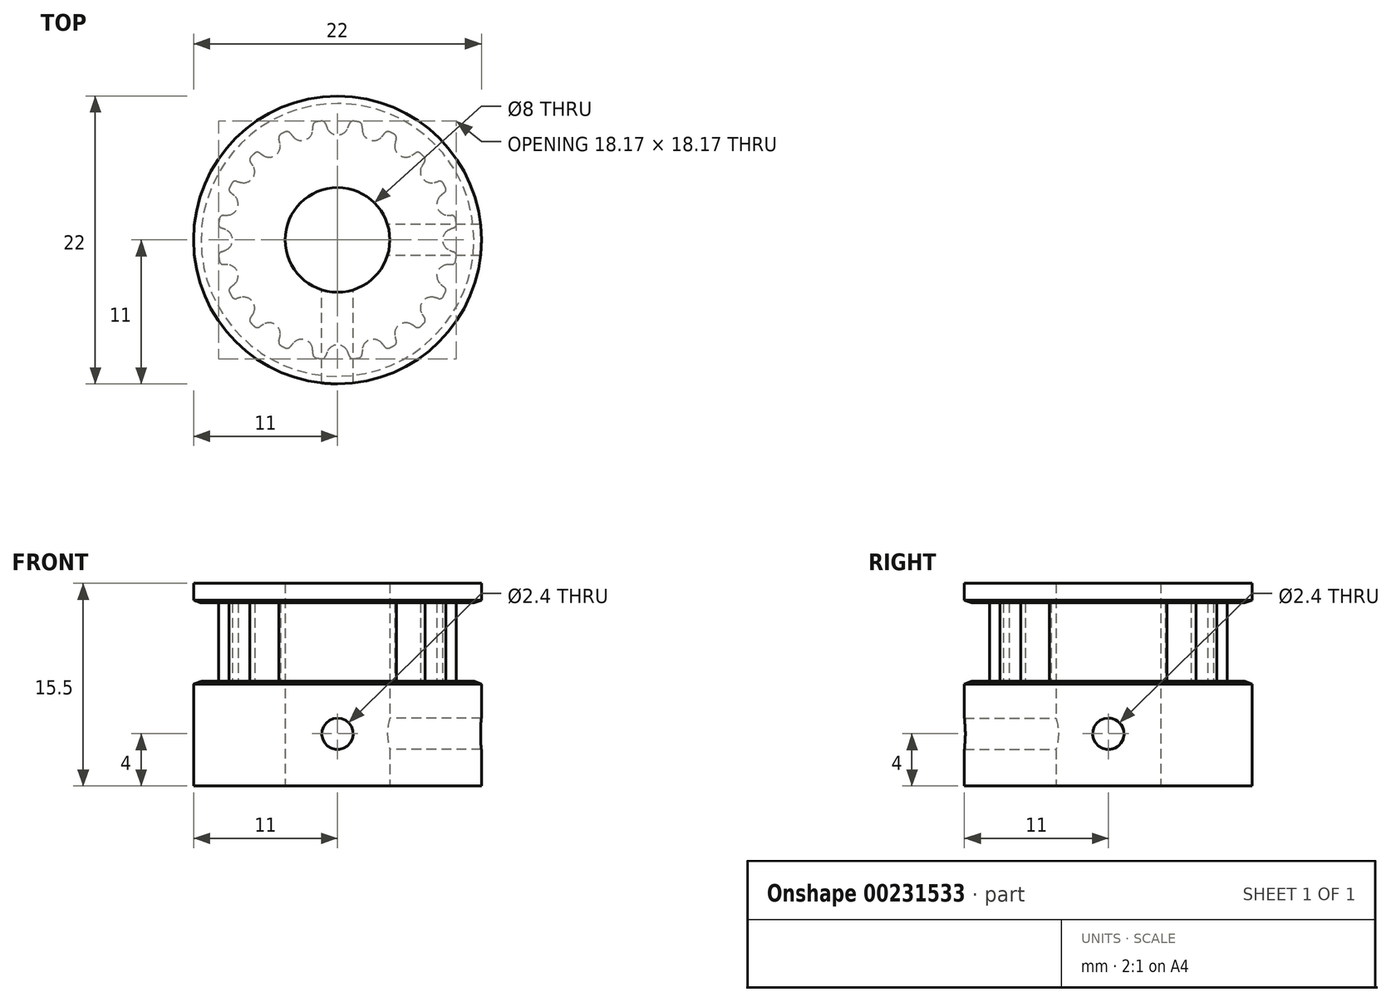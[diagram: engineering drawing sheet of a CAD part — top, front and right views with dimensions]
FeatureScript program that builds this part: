
annotation { "Feature Type Name" : "Feature", "Feature Type Description" : "" }
export const myFeature = defineFeature(function(context is Context, id is Id, definition is map)
    precondition{}
    {
        {
            assignVariable(context, id + "F0", {"name" : "teeth", "anyValue" : 20});
        }
        {
            assignVariable(context, id + "F1", {"name" : "belt_width", "anyValue" : 6 * mm});
        }
        {
            assignVariable(context, id + "F2", {"name" : "bore_diameter", "anyValue" : 8 * mm});
        }
        {
            var Q0;
            Q0=qCreatedBy(makeId("Top.planeOp"),FACE);
            var sketch = newSketch(context, id + "F3", { "sketchPlane" : qUnion([Q0])});
            skLineSegment(sketch, "E0", {"start": v(0, 0) * mm, "end": v(0, 8.03) * mm, "construction": true});
            skCircle(sketch, "E1", {"center": v(0, 0) * mm, "radius": 9.17 * mm});
            skPoint(sketch, "E2.MirrorCS.end.orphan", {"position": v(1.43, 9.06) * mm});
            skLineSegment(sketch, "E3", {"start": v(1.43, 9.06) * mm, "end": v(1.5, 9.43) * mm, "construction": true});
            skLineSegment(sketch, "E4", {"start": v(-1.43, 9.06) * mm, "end": v(-1.5, 9.43) * mm, "construction": true});
            skArc(sketch, "E5", {"start": v(0, 8.03) * mm, "mid": v(0.47, 8.17) * mm, "end": v(0.79, 8.55) * mm});
            skArc(sketch, "E6", {"start": v(0.79, 8.55) * mm, "mid": v(0.84, 8.72) * mm, "end": v(0.88, 8.89) * mm, "construction": true});
            skLineSegment(sketch, "E7", {"start": v(0, 8.03) * mm, "end": v(0, 9.17) * mm, "construction": true});
            skLineSegment(sketch, "E8", {"start": v(0, 9.17) * mm, "end": v(0, 9.55) * mm, "construction": true});
            skArc(sketch, "E9", {"start": v(0.88, 8.89) * mm, "mid": v(0.98, 9.05) * mm, "end": v(1.16, 9.1) * mm, "construction": true});
            skArc(sketch, "E10", {"start": v(1.5, 9.43) * mm, "mid": v(0, 9.55) * mm, "end": v(-1.5, 9.43) * mm, "construction": true});
            skLineSegment(sketch, "E11", {"start": v(1.43, 9.06) * mm, "end": v(1.26, 7.93) * mm});
            skLineSegment(sketch, "E12", {"start": v(1.26, 7.93) * mm, "end": v(0, 0) * mm});
            skLineSegment(sketch, "E13", {"start": v(0, 0) * mm, "end": v(-1.26, 7.93) * mm});
            skLineSegment(sketch, "E14", {"start": v(-1.26, 7.93) * mm, "end": v(-1.43, 9.06) * mm});
            skArc(sketch, "E15", {"start": v(1.25, 9.08) * mm, "mid": v(1.04, 9.04) * mm, "end": v(0.91, 8.88) * mm});
            skArc(sketch, "E16", {"start": v(0.79, 8.55) * mm, "mid": v(0.85, 8.72) * mm, "end": v(0.91, 8.88) * mm});
            skArc(sketch, "E17.MirrorCS", {"start": v(0, 8.03) * mm, "mid": v(-0.47, 8.17) * mm, "end": v(-0.79, 8.55) * mm});
            skArc(sketch, "E18.MirrorCS", {"start": v(-0.79, 8.55) * mm, "mid": v(-0.85, 8.72) * mm, "end": v(-0.91, 8.88) * mm});
            skArc(sketch, "E19.MirrorCS", {"start": v(-1.25, 9.08) * mm, "mid": v(-1.04, 9.04) * mm, "end": v(-0.91, 8.88) * mm});
            skArc(sketch, "E20", {"start": v(0, 9.17) * mm, "mid": v(-0.3, 9.16) * mm, "end": v(-0.61, 9.15) * mm});
            skArc(sketch, "E21", {"start": v(1.26, 7.93) * mm, "mid": v(0, 8.03) * mm, "end": v(-1.26, 7.93) * mm, "construction": true});
            skLineSegment(sketch, "E22", {"start": v(1.5, 9.43) * mm, "end": v(1.63, 10.3) * mm, "construction": true});
            skLineSegment(sketch, "E23", {"start": v(-1.5, 9.43) * mm, "end": v(-1.63, 10.3) * mm, "construction": true});
            skArc(sketch, "E24", {"start": v(1.63, 10.3) * mm, "mid": v(0, 10.43) * mm, "end": v(-1.63, 10.3) * mm, "construction": true});
            skSolve(sketch);
        }
        {
            var Q0;
            Q0=makeQuery(id+"F3.imprint","IMPRINT",FACE,{"disambiguationData":[TD([[makeQuery(id+"F3.imprint","IMPRINT",EDGE,{"derivedFrom":sQuery(id+"F3.wireOp",EDGE,"E5")}),-1.0]])]});
            var Q1;
            {var subQ1=sQuery(id+"F3.wireOp",EDGE,"E14");Q1=makeQuery(id+"F3.imprint","IMPRINT",FACE,{"disambiguationData":[TD([[makeQuery(id+"F3.imprint","IMPRINT",EDGE,{"derivedFrom":subQ1}),-1.0]])]});}
            var Q2;
            {var subQ0=sQuery(id+"F3.wireOp",EDGE,"E12");Q2=makeQuery(id+"F3.imprint","IMPRINT",FACE,{"disambiguationData":[TD([[makeQuery(id+"F3.imprint","IMPRINT",EDGE,{"derivedFrom":subQ0}),-1.0]])]});}
            extrude(context, id + "F4", {"entities" : qUnion([Q0, Q1, Q2]), "endBound" : BoundingType.SYMMETRIC, "depth" : getVariable(context, 'belt_width')});
        }
        {
            var Q0;
            Q0=makeQuery(id+"F4.opExtrude","SWEPT_BODY",BODY,{"disambiguationData":[OSD([sQuery(id+"F3.wireOp",EDGE,"E1"),sQuery(id+"F3.wireOp",EDGE,"E5"),sQuery(id+"F3.wireOp",EDGE,"E11"),sQuery(id+"F3.wireOp",EDGE,"E12"),sQuery(id+"F3.wireOp",EDGE,"E13"),sQuery(id+"F3.wireOp",EDGE,"E14"),sQuery(id+"F3.wireOp",EDGE,"E15"),sQuery(id+"F3.wireOp",EDGE,"E16"),sQuery(id+"F3.wireOp",EDGE,"E17.MirrorCS"),sQuery(id+"F3.wireOp",EDGE,"E18.MirrorCS"),sQuery(id+"F3.wireOp",EDGE,"E19.MirrorCS")])]});
            var Q1;
            Q1=makeQuery(id+"F4.opExtrude","SWEPT_EDGE",EDGE,{"disambiguationData":[OSD([sQuery(id+"F3.wireOp",EDGE,"E12"),sQuery(id+"F3.wireOp",EDGE,"E13")])]});
            circularPattern(context, id + "F5", {"operationType" : NewBodyOperationType.ADD, "entities" : qUnion([Q0]), "axis" : qUnion([Q1]), "angle" : 360 * degree, "instanceCount" : getVariable(context, 'teeth'), "equalSpace" : true});
        }
        {
            var Q0;
            Q0=qCreatedBy(makeId("Front.planeOp"),FACE);
            var sketch = newSketch(context, id + "F6", { "sketchPlane" : qUnion([Q0])});
            skLineSegment(sketch, "E25", {"start": v(0, -3) * mm, "end": v(10.43, -3) * mm});
            skLineSegment(sketch, "E26", {"start": v(10.43, -3) * mm, "end": v(11, -3.2) * mm});
            skLineSegment(sketch, "E27", {"start": v(11, -3.2) * mm, "end": v(11, -11) * mm});
            skLineSegment(sketch, "E28", {"start": v(11, -11) * mm, "end": v(0, -11) * mm});
            skLineSegment(sketch, "E29", {"start": v(0, -11) * mm, "end": v(0, -3) * mm});
            skLineSegment(sketch, "E30", {"start": v(0, 3) * mm, "end": v(10.43, 3) * mm});
            skLineSegment(sketch, "E31", {"start": v(11, 3.2) * mm, "end": v(10.43, 3) * mm});
            skLineSegment(sketch, "E32", {"start": v(11, 3.2) * mm, "end": v(11, 4.5) * mm});
            skLineSegment(sketch, "E33", {"start": v(11, 4.5) * mm, "end": v(0, 4.5) * mm});
            skLineSegment(sketch, "E34", {"start": v(0, 4.5) * mm, "end": v(0, 3) * mm});
            skLineSegment(sketch, "E35", {"start": v(10.43, -3) * mm, "end": v(11, -3) * mm, "construction": true});
            skLineSegment(sketch, "E36", {"start": v(11, -3) * mm, "end": v(11, -3.2) * mm, "construction": true});
            skLineSegment(sketch, "E37", {"start": v(10.43, 3) * mm, "end": v(11, 3) * mm, "construction": true});
            skLineSegment(sketch, "E38", {"start": v(11, 3) * mm, "end": v(11, 3.2) * mm, "construction": true});
            skLineSegment(sketch, "E39", {"start": v(9.17, -3) * mm, "end": v(9.17, 0) * mm, "construction": true});
            skSolve(sketch);
        }
        {
            var Q0;
            Q0=qSketchRegion(id+"F6",true);
            var Q1;
            Q1=qConstructionFilter(qBodyType(qCreatedBy(id+"F6",EDGE),BodyType.WIRE),ConstructionObject.NO);
            var Q2;
            Q2=sQuery(id+"F6.wireOp",EDGE,"E29");
            revolve(context, id + "F7", {"operationType" : NewBodyOperationType.ADD, "entities" : qUnion([Q0]), "surfaceEntities" : qUnion([Q1]), "axis" : qUnion([Q2]), "revolveType" : RevolveType.FULL});
        }
        {
            var Q0;
            Q0=makeQuery(id+"F7.opRevolve","SWEPT_FACE",FACE,{"disambiguationData":[OSD([sQuery(id+"F6.wireOp",EDGE,"E28")])]});
            var sketch = newSketch(context, id + "F8", { "sketchPlane" : qUnion([Q0])});
            skPoint(sketch, "E40", {"position": v(0, 0) * mm});
            skSolve(sketch);
        }
        {
            var Q0;
            Q0=sQuery(id+"F8.wireOp",VERTEX,"E40");
            var Q1;
            Q1=makeQuery(id+"F4.opExtrude","SWEPT_BODY",BODY,{"disambiguationData":[OSD([sQuery(id+"F3.wireOp",EDGE,"E1"),sQuery(id+"F3.wireOp",EDGE,"E5"),sQuery(id+"F3.wireOp",EDGE,"E11"),sQuery(id+"F3.wireOp",EDGE,"E12"),sQuery(id+"F3.wireOp",EDGE,"E13"),sQuery(id+"F3.wireOp",EDGE,"E14"),sQuery(id+"F3.wireOp",EDGE,"E15"),sQuery(id+"F3.wireOp",EDGE,"E16"),sQuery(id+"F3.wireOp",EDGE,"E17.MirrorCS"),sQuery(id+"F3.wireOp",EDGE,"E18.MirrorCS"),sQuery(id+"F3.wireOp",EDGE,"E19.MirrorCS")])]});
            hole(context, id + "F9", {"style" : HoleStyle.SIMPLE, "holeDiameter" : getVariable(context, 'bore_diameter'), "endStyle" : HoleEndStyle.THROUGH, "locations" : qUnion([Q0]), "scope" : qUnion([Q1]), "isTappedThrough" : true});
        }
        {
            var Q0;
            Q0=qCreatedBy(makeId("Front.planeOp"),FACE);
            var sketch = newSketch(context, id + "F10", { "sketchPlane" : qUnion([Q0])});
            skPoint(sketch, "E41", {"position": v(0, -7) * mm});
            skLineSegment(sketch, "E42", {"start": v(0, -11) * mm, "end": v(0, -3) * mm});
            skSolve(sketch);
        }
        {
            var Q0;
            Q0=qCreatedBy(makeId("Right.planeOp"),FACE);
            var sketch = newSketch(context, id + "F11", { "sketchPlane" : qUnion([Q0])});
            skPoint(sketch, "E43", {"position": v(0, -7) * mm});
            skSolve(sketch);
        }
        {
            var Q0;
            Q0=sQuery(id+"F10.wireOp",VERTEX,"E41");
            var Q1;
            Q1=makeQuery(id+"F4.opExtrude","SWEPT_BODY",BODY,{"disambiguationData":[OSD([sQuery(id+"F3.wireOp",EDGE,"E1"),sQuery(id+"F3.wireOp",EDGE,"E5"),sQuery(id+"F3.wireOp",EDGE,"E11"),sQuery(id+"F3.wireOp",EDGE,"E12"),sQuery(id+"F3.wireOp",EDGE,"E13"),sQuery(id+"F3.wireOp",EDGE,"E14"),sQuery(id+"F3.wireOp",EDGE,"E15"),sQuery(id+"F3.wireOp",EDGE,"E16"),sQuery(id+"F3.wireOp",EDGE,"E17.MirrorCS"),sQuery(id+"F3.wireOp",EDGE,"E18.MirrorCS"),sQuery(id+"F3.wireOp",EDGE,"E19.MirrorCS")])]});
            hole(context, id + "F12", {"style" : HoleStyle.SIMPLE, "endStyle" : HoleEndStyle.THROUGH, "oppositeDirection" : true, "standardTappedOrClearance" : lookupTablePath({ "standard" : "ISO", "engagement" : "75%", "pitch" : "0.6 mm", "size" : "M3", "type" : "Tapped" }), "standardBlindInLast" : lookupTablePath({ "standard" : "ISO", "engagement" : "75%", "pitch" : "0.6 mm", "size" : "M3", "type" : "Tapped" }), "holeDiameter" : 2.4 * mm, "locations" : qUnion([Q0]), "scope" : qUnion([Q1]), "isTappedThrough" : true, "showTappedDepth" : true});
        }
        {
            var Q0;
            Q0=sQuery(id+"F11.wireOp",VERTEX,"E43");
            var Q1;
            Q1=makeQuery(id+"F4.opExtrude","SWEPT_BODY",BODY,{"disambiguationData":[OSD([sQuery(id+"F3.wireOp",EDGE,"E1"),sQuery(id+"F3.wireOp",EDGE,"E5"),sQuery(id+"F3.wireOp",EDGE,"E11"),sQuery(id+"F3.wireOp",EDGE,"E12"),sQuery(id+"F3.wireOp",EDGE,"E13"),sQuery(id+"F3.wireOp",EDGE,"E14"),sQuery(id+"F3.wireOp",EDGE,"E15"),sQuery(id+"F3.wireOp",EDGE,"E16"),sQuery(id+"F3.wireOp",EDGE,"E17.MirrorCS"),sQuery(id+"F3.wireOp",EDGE,"E18.MirrorCS"),sQuery(id+"F3.wireOp",EDGE,"E19.MirrorCS")])]});
            hole(context, id + "F13", {"style" : HoleStyle.SIMPLE, "endStyle" : HoleEndStyle.THROUGH, "oppositeDirection" : true, "standardTappedOrClearance" : lookupTablePath({ "standard" : "ISO", "engagement" : "75%", "pitch" : "0.6 mm", "size" : "M3", "type" : "Tapped" }), "standardBlindInLast" : lookupTablePath({ "standard" : "ISO", "engagement" : "75%", "pitch" : "0.6 mm", "size" : "M3", "type" : "Tapped" }), "holeDiameter" : 2.4 * mm, "locations" : qUnion([Q0]), "scope" : qUnion([Q1]), "isTappedThrough" : true, "showTappedDepth" : true});
        }
    });
